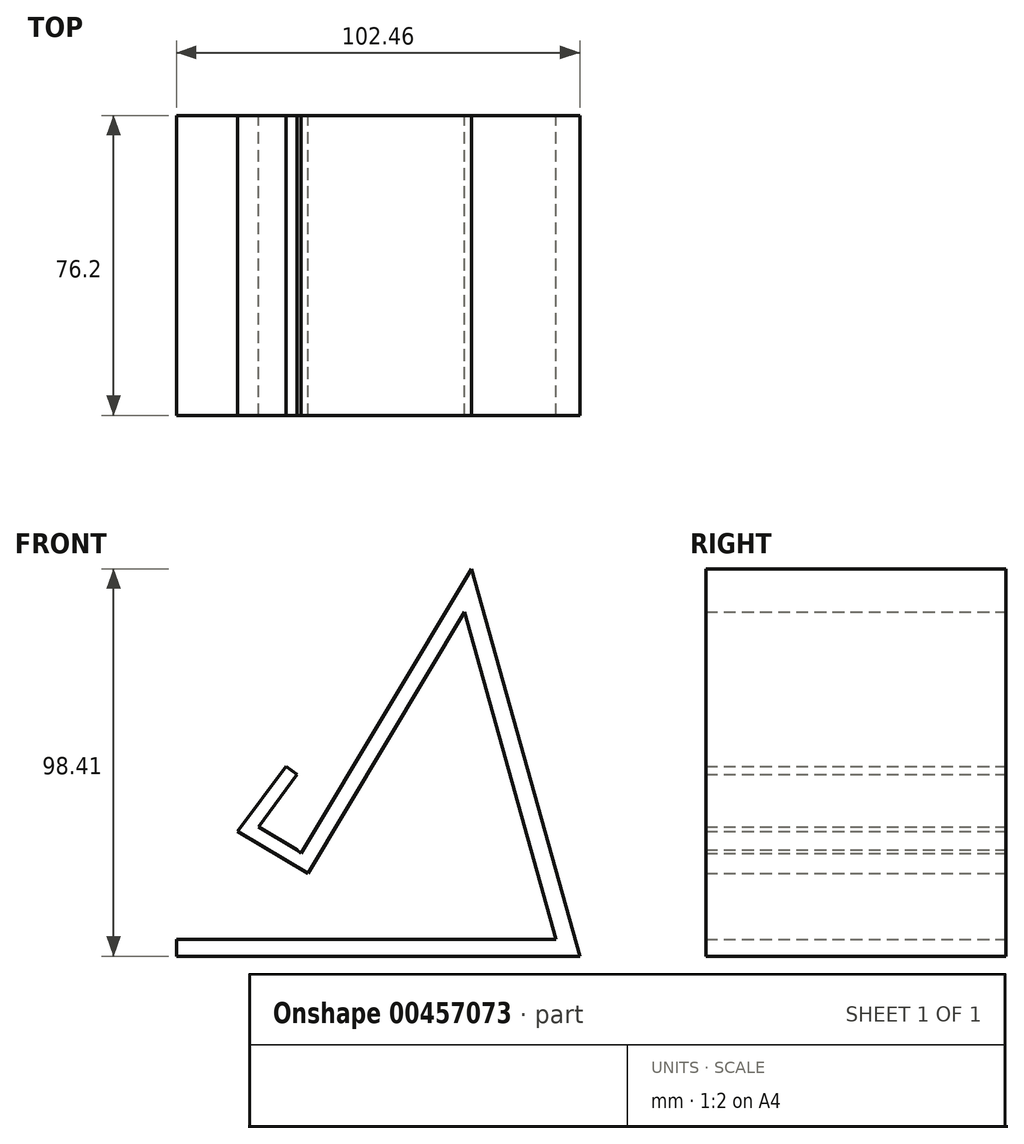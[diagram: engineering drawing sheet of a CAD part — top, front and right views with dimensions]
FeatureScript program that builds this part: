
annotation { "Feature Type Name" : "Feature", "Feature Type Description" : "" }
export const myFeature = defineFeature(function(context is Context, id is Id, definition is map)
    precondition{}
    {
        {
            var Q0;
            Q0=qCreatedBy(makeId("Front.planeOp"),FACE);
            var sketch = newSketch(context, id + "F0", { "sketchPlane" : qUnion([Q0])});
            skLineSegment(sketch, "E0", {"start": v(-46.91, -27.34) * mm, "end": v(49.5, -27.34) * mm});
            skLineSegment(sketch, "E1", {"start": v(-46.91, -27.34) * mm, "end": v(-46.91, -31.66) * mm});
            skLineSegment(sketch, "E2", {"start": v(-46.91, -31.66) * mm, "end": v(55.55, -31.66) * mm});
            skLineSegment(sketch, "E3", {"start": v(55.55, -31.66) * mm, "end": v(31.95, 52.67) * mm});
            skLineSegment(sketch, "E4", {"start": v(49.5, -27.34) * mm, "end": v(30.5, 40.58) * mm});
            skLineSegment(sketch, "E5", {"start": v(31.95, 52.67) * mm, "end": v(28, 66.75) * mm});
            skLineSegment(sketch, "E6", {"start": v(28, 66.75) * mm, "end": v(-13.53, -2.6) * mm});
            skLineSegment(sketch, "E7", {"start": v(30.5, 40.58) * mm, "end": v(27.11, 52.67) * mm});
            skLineSegment(sketch, "E8", {"start": v(27.11, 52.67) * mm, "end": v(26.26, 55.72) * mm});
            skLineSegment(sketch, "E9", {"start": v(26.26, 55.72) * mm, "end": v(-13.53, -10.7) * mm});
            skLineSegment(sketch, "E10", {"start": v(-13.53, -10.7) * mm, "end": v(-31.38, 0) * mm});
            skLineSegment(sketch, "E11", {"start": v(-31.38, 0) * mm, "end": v(-19.13, 16.6) * mm});
            skLineSegment(sketch, "E12", {"start": v(-19.13, 16.6) * mm, "end": v(-16.23, 14.45) * mm});
            skLineSegment(sketch, "E13", {"start": v(-16.23, 14.45) * mm, "end": v(-25.06, 2.47) * mm});
            skLineSegment(sketch, "E14", {"start": v(-25.06, 2.47) * mm, "end": v(-26.02, 1.18) * mm});
            skLineSegment(sketch, "E15", {"start": v(-26.02, 1.18) * mm, "end": v(-16.23, -4.68) * mm});
            skLineSegment(sketch, "E16", {"start": v(-13.53, -2.6) * mm, "end": v(-15.3, -5.55) * mm});
            skLineSegment(sketch, "E17", {"start": v(-16.23, -4.68) * mm, "end": v(-15.3, -5.55) * mm});
            skSolve(sketch);
        }
        {
            var Q0;
            Q0=makeQuery(id+"F0.imprint","IMPRINT",FACE,{"disambiguationData":[TD([[makeQuery(id+"F0.imprint","IMPRINT",EDGE,{"derivedFrom":sQuery(id+"F0.wireOp",EDGE,"E0")}),-1.0]])]});
            extrude(context, id + "F1", {"entities" : qUnion([Q0]), "depth" : 25.4 * mm});
        }
        {
            var Q0;
            Q0=makeQuery(id+"F1.opExtrude","CAP_FACE",FACE,{"disambiguationData":[OSD([sQuery(id+"F0.wireOp",EDGE,"E0"),sQuery(id+"F0.wireOp",EDGE,"E1"),sQuery(id+"F0.wireOp",EDGE,"E2"),sQuery(id+"F0.wireOp",EDGE,"E3"),sQuery(id+"F0.wireOp",EDGE,"E4"),sQuery(id+"F0.wireOp",EDGE,"E5"),sQuery(id+"F0.wireOp",EDGE,"E6"),sQuery(id+"F0.wireOp",EDGE,"E7"),sQuery(id+"F0.wireOp",EDGE,"E8"),sQuery(id+"F0.wireOp",EDGE,"E9"),sQuery(id+"F0.wireOp",EDGE,"E10"),sQuery(id+"F0.wireOp",EDGE,"E11"),sQuery(id+"F0.wireOp",EDGE,"E12"),sQuery(id+"F0.wireOp",EDGE,"E13"),sQuery(id+"F0.wireOp",EDGE,"E14"),sQuery(id+"F0.wireOp",EDGE,"E15"),sQuery(id+"F0.wireOp",EDGE,"E16"),sQuery(id+"F0.wireOp",EDGE,"E17")])],"isStart":false});
            extrude(context, id + "F2", {"entities" : qUnion([Q0]), "operationType" : NewBodyOperationType.ADD, "depth" : 50.8 * mm});
        }
    });
